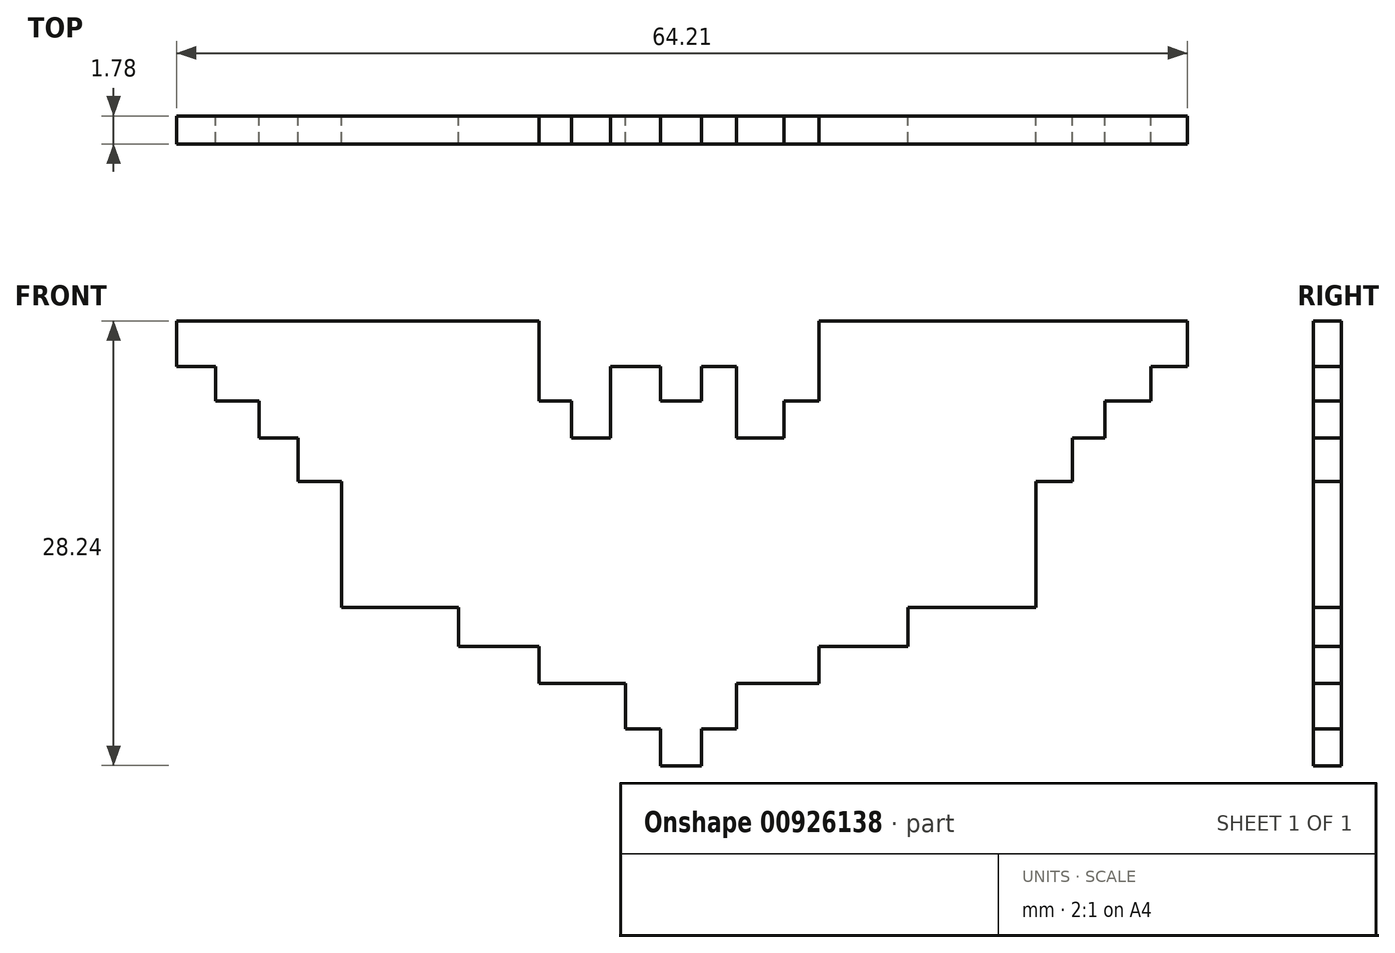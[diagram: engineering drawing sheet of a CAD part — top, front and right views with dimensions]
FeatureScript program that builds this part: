
annotation { "Feature Type Name" : "Feature", "Feature Type Description" : "" }
export const myFeature = defineFeature(function(context is Context, id is Id, definition is map)
    precondition{}
    {
        {
            var Q0;
            Q0=qCreatedBy(makeId("Front.planeOp"),FACE);
            var sketch = newSketch(context, id + "F0", { "sketchPlane" : qUnion([Q0])});
            skLineSegment(sketch, "E0", {"start": v(-16.28, 24.76) * mm, "end": v(6.73, 24.76) * mm});
            skLineSegment(sketch, "E1", {"start": v(6.73, 19.66) * mm, "end": v(8.8, 19.66) * mm});
            skLineSegment(sketch, "E2", {"start": v(6.73, 24.76) * mm, "end": v(6.73, 19.66) * mm});
            skLineSegment(sketch, "E3", {"start": v(8.8, 19.66) * mm, "end": v(8.8, 17.32) * mm});
            skLineSegment(sketch, "E4", {"start": v(8.8, 17.32) * mm, "end": v(11.28, 17.32) * mm});
            skLineSegment(sketch, "E5", {"start": v(11.28, 21.87) * mm, "end": v(11.28, 17.32) * mm});
            skLineSegment(sketch, "E6", {"start": v(11.28, 21.87) * mm, "end": v(14.45, 21.87) * mm});
            skLineSegment(sketch, "E7", {"start": v(14.45, 21.87) * mm, "end": v(14.45, 19.66) * mm});
            skLineSegment(sketch, "E8", {"start": v(17.06, 19.66) * mm, "end": v(14.45, 19.66) * mm});
            skLineSegment(sketch, "E9", {"start": v(17.06, 19.66) * mm, "end": v(17.06, 21.87) * mm});
            skLineSegment(sketch, "E10", {"start": v(19.27, 21.87) * mm, "end": v(19.27, 17.32) * mm});
            skLineSegment(sketch, "E11", {"start": v(19.27, 17.32) * mm, "end": v(22.3, 17.32) * mm});
            skLineSegment(sketch, "E12", {"start": v(22.3, 17.32) * mm, "end": v(22.3, 19.66) * mm});
            skLineSegment(sketch, "E13", {"start": v(22.3, 19.66) * mm, "end": v(24.5, 19.66) * mm});
            skLineSegment(sketch, "E14", {"start": v(24.5, 19.66) * mm, "end": v(24.5, 24.76) * mm});
            skLineSegment(sketch, "E15", {"start": v(24.5, 24.76) * mm, "end": v(47.93, 24.76) * mm});
            skLineSegment(sketch, "E16", {"start": v(47.93, 24.76) * mm, "end": v(47.93, 21.87) * mm});
            skLineSegment(sketch, "E17", {"start": v(47.93, 21.87) * mm, "end": v(45.58, 21.87) * mm});
            skLineSegment(sketch, "E18", {"start": v(45.58, 21.87) * mm, "end": v(45.58, 19.66) * mm});
            skLineSegment(sketch, "E19", {"start": v(45.58, 19.66) * mm, "end": v(42.7, 19.66) * mm});
            skLineSegment(sketch, "E20", {"start": v(42.7, 19.66) * mm, "end": v(42.7, 17.32) * mm});
            skLineSegment(sketch, "E21", {"start": v(42.7, 17.32) * mm, "end": v(40.62, 17.32) * mm});
            skLineSegment(sketch, "E22", {"start": v(40.62, 17.32) * mm, "end": v(40.62, 14.57) * mm});
            skLineSegment(sketch, "E23", {"start": v(40.62, 14.57) * mm, "end": v(38.28, 14.57) * mm});
            skLineSegment(sketch, "E24", {"start": v(38.28, 14.57) * mm, "end": v(38.28, 6.58) * mm});
            skLineSegment(sketch, "E25", {"start": v(38.28, 6.58) * mm, "end": v(30.15, 6.58) * mm});
            skLineSegment(sketch, "E26", {"start": v(30.15, 6.58) * mm, "end": v(30.15, 4.1) * mm});
            skLineSegment(sketch, "E27", {"start": v(30.15, 4.1) * mm, "end": v(24.5, 4.1) * mm});
            skLineSegment(sketch, "E28", {"start": v(24.5, 4.1) * mm, "end": v(24.5, 1.75) * mm});
            skLineSegment(sketch, "E29", {"start": v(24.5, 1.75) * mm, "end": v(19.27, 1.75) * mm});
            skLineSegment(sketch, "E30", {"start": v(19.27, 1.75) * mm, "end": v(19.27, -1.14) * mm});
            skLineSegment(sketch, "E31", {"start": v(19.27, -1.14) * mm, "end": v(17.06, -1.14) * mm});
            skLineSegment(sketch, "E32", {"start": v(17.06, -1.14) * mm, "end": v(17.06, -3.48) * mm});
            skLineSegment(sketch, "E33", {"start": v(17.06, -3.48) * mm, "end": v(14.45, -3.48) * mm});
            skLineSegment(sketch, "E34", {"start": v(14.45, -3.48) * mm, "end": v(14.45, -1.14) * mm});
            skLineSegment(sketch, "E35", {"start": v(14.45, -1.14) * mm, "end": v(12.24, -1.14) * mm});
            skLineSegment(sketch, "E36", {"start": v(12.24, -1.14) * mm, "end": v(12.24, 1.75) * mm});
            skLineSegment(sketch, "E37", {"start": v(12.24, 1.75) * mm, "end": v(6.73, 1.75) * mm});
            skLineSegment(sketch, "E38", {"start": v(6.73, 1.75) * mm, "end": v(6.73, 4.1) * mm});
            skLineSegment(sketch, "E39", {"start": v(6.73, 4.1) * mm, "end": v(1.63, 4.1) * mm});
            skLineSegment(sketch, "E40", {"start": v(1.63, 4.1) * mm, "end": v(1.63, 6.58) * mm});
            skLineSegment(sketch, "E41", {"start": v(1.63, 6.58) * mm, "end": v(-5.8, 6.58) * mm});
            skLineSegment(sketch, "E42", {"start": v(-5.8, 6.58) * mm, "end": v(-5.8, 14.57) * mm});
            skLineSegment(sketch, "E43", {"start": v(-5.8, 14.57) * mm, "end": v(-8.56, 14.57) * mm});
            skLineSegment(sketch, "E44", {"start": v(-8.56, 14.57) * mm, "end": v(-8.56, 17.32) * mm});
            skLineSegment(sketch, "E45", {"start": v(-8.56, 17.32) * mm, "end": v(-11.04, 17.32) * mm});
            skLineSegment(sketch, "E46", {"start": v(-11.04, 17.32) * mm, "end": v(-11.04, 19.66) * mm});
            skLineSegment(sketch, "E47", {"start": v(-11.04, 19.66) * mm, "end": v(-13.8, 19.66) * mm});
            skLineSegment(sketch, "E48", {"start": v(-13.8, 19.66) * mm, "end": v(-13.8, 21.87) * mm});
            skLineSegment(sketch, "E49", {"start": v(-13.8, 21.87) * mm, "end": v(-16.28, 21.87) * mm});
            skLineSegment(sketch, "E50", {"start": v(-16.28, 21.87) * mm, "end": v(-16.28, 24.76) * mm});
            skLineSegment(sketch, "E51", {"start": v(17.06, 21.87) * mm, "end": v(19.27, 21.87) * mm});
            skSolve(sketch);
        }
        {
            var Q0;
            Q0 = qSketchRegion(id + "F0", true);
            extrude(context, id + "F1", {"entities" : qUnion([Q0]), "depth" : 1.78 * mm, "offsetDistance" : 25.4 * mm});
        }
    });
